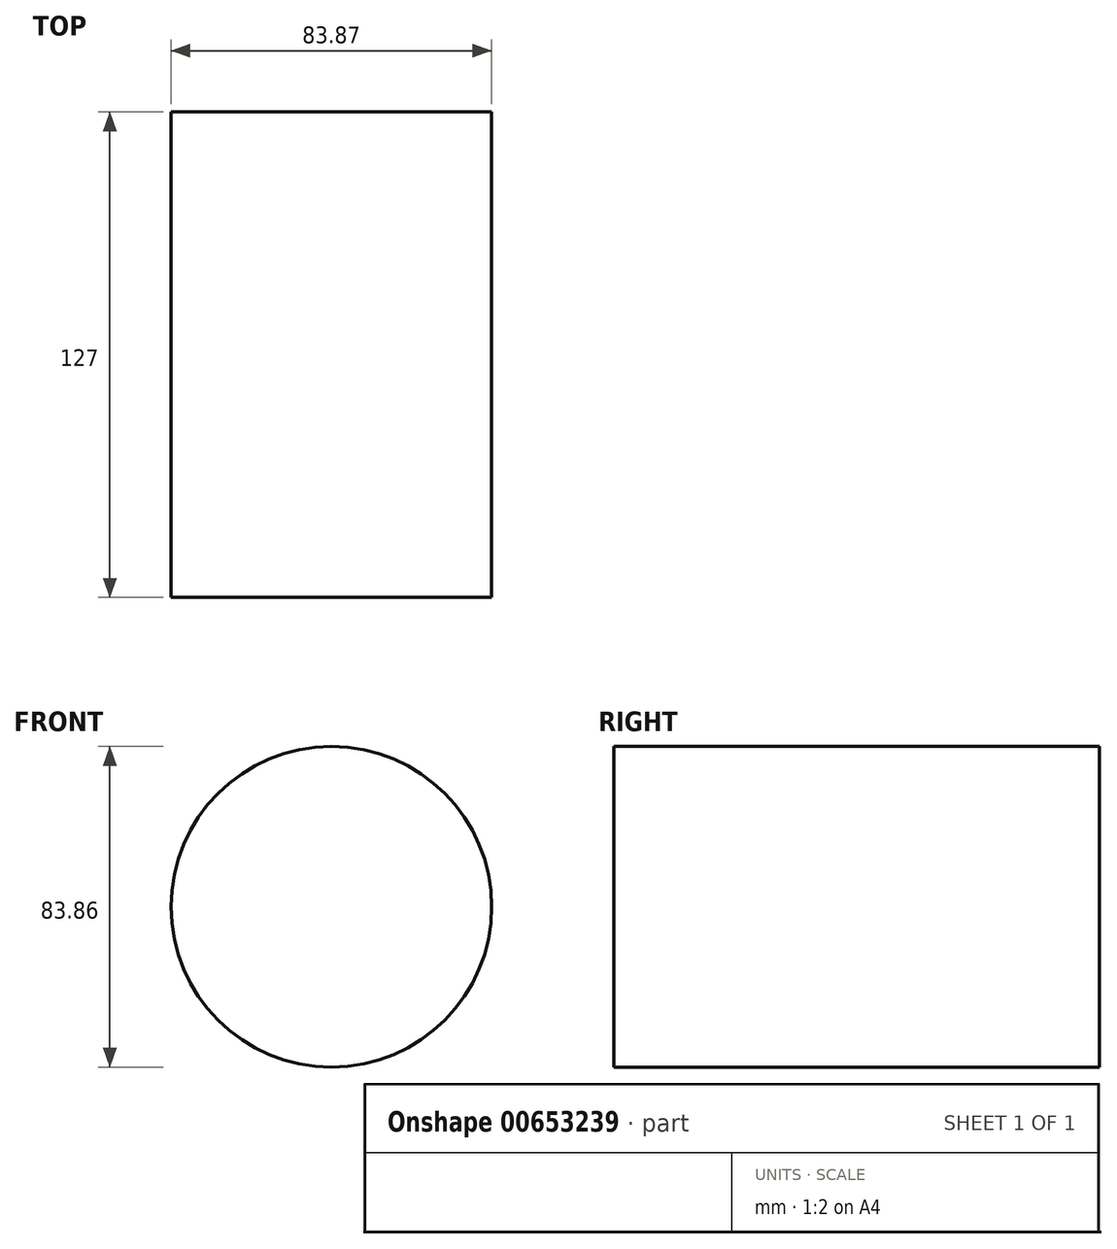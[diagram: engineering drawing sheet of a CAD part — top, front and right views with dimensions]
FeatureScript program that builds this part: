
annotation { "Feature Type Name" : "Feature", "Feature Type Description" : "" }
export const myFeature = defineFeature(function(context is Context, id is Id, definition is map)
    precondition{}
    {
        {
            var Q0;
            Q0=qCreatedBy(makeId("Front.planeOp"),FACE);
            var sketch = newSketch(context, id + "F0", { "sketchPlane" : qUnion([Q0])});
            skCircle(sketch, "E0", {"center": v(16.16, 22.25) * mm, "radius": 41.93 * mm});
            skLineSegment(sketch, "E1", {"start": v(58.08, 22.99) * mm, "end": v(58.08, -40.74) * mm});
            skLineSegment(sketch, "E2", {"start": v(58.08, -40.74) * mm, "end": v(-27.8, -42.6) * mm});
            skLineSegment(sketch, "E3", {"start": v(-27.8, -42.6) * mm, "end": v(-25.78, 21.53) * mm});
            skSolve(sketch);
        }
        {
            var Q0;
            {var subQ0=sQuery(id+"F0.wireOp",EDGE,"E1");var subQ1=sQuery(id+"F0.wireOp",EDGE,"E0");var subQ2=makeQuery(id+"F0.imprint","INTERSECT",VERTEX,{"disambiguationData":[OD(0.0)],"derivedFrom":[subQ1,subQ0]});Q0=makeQuery(id+"F0.imprint","IMPRINT",FACE,{"disambiguationData":[TD([[makeQuery(id+"F0.imprint","IMPRINT",EDGE,{"disambiguationData":[TD([[subQ2,1.0]])],"derivedFrom":subQ1}),1.0]])]});}
            var Q1;
            {var subQ0=sQuery(id+"F0.wireOp",EDGE,"E1");var subQ1=sQuery(id+"F0.wireOp",EDGE,"E0");var subQ2=makeQuery(id+"F0.imprint","INTERSECT",VERTEX,{"disambiguationData":[OD(0.0)],"derivedFrom":[subQ1,subQ0]});Q1=makeQuery(id+"F0.imprint","IMPRINT",FACE,{"disambiguationData":[TD([[makeQuery(id+"F0.imprint","IMPRINT",EDGE,{"disambiguationData":[TD([[subQ2,-1.0]])],"derivedFrom":subQ1}),1.0]])]});}
            extrude(context, id + "F1", {"entities" : qUnion([Q0, Q1]), "depth" : 127 * mm, "offsetDistance" : 25.4 * mm});
        }
    });
